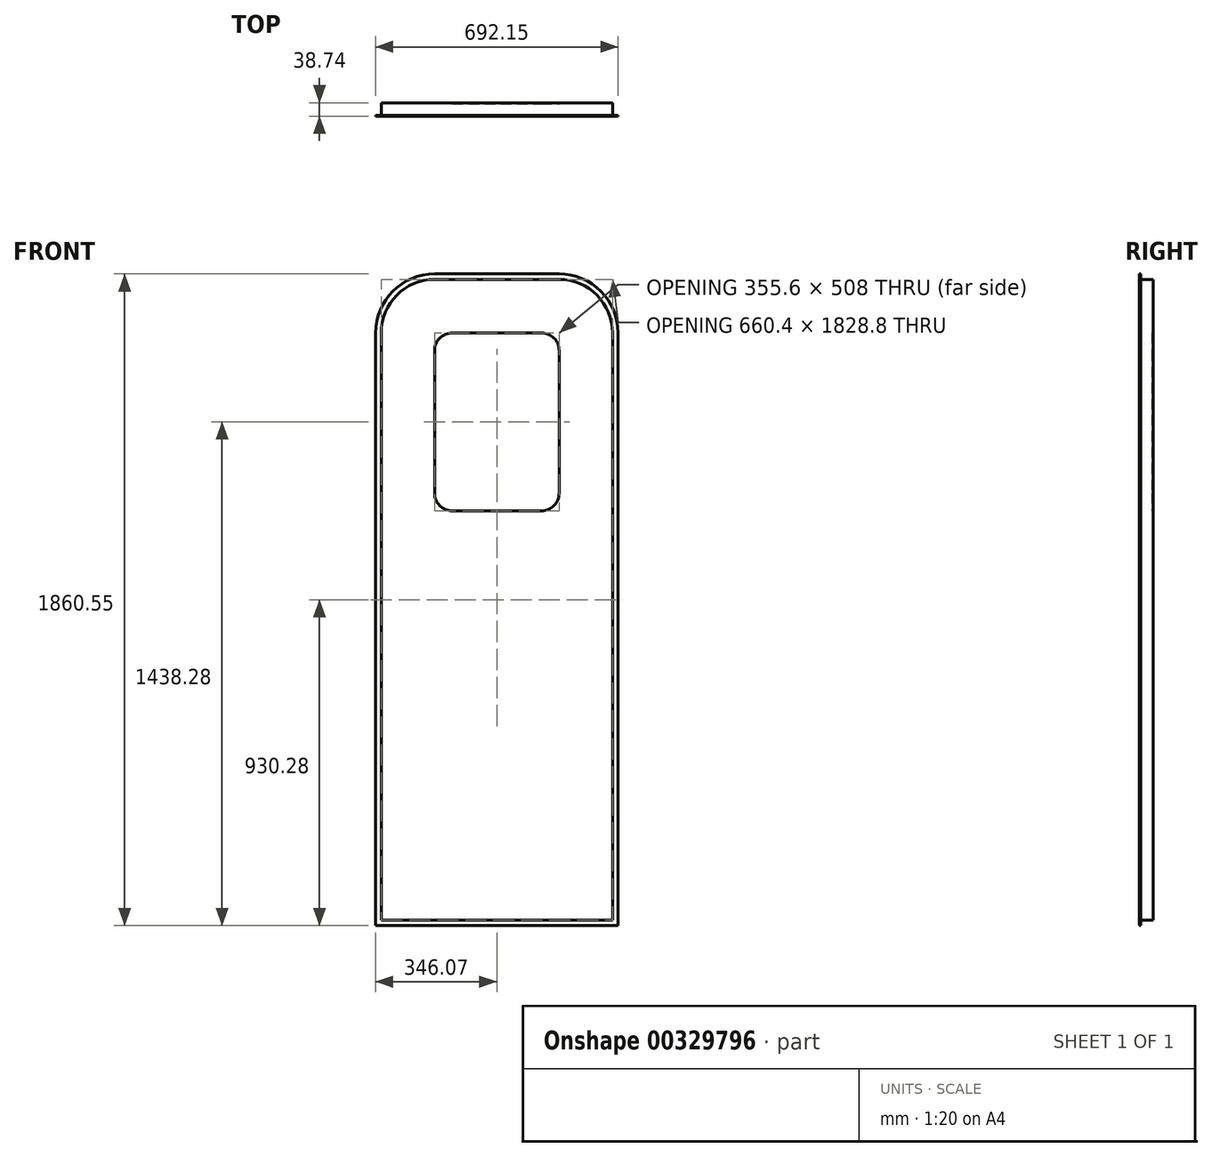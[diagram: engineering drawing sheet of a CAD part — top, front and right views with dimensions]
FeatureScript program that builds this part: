
annotation { "Feature Type Name" : "Feature", "Feature Type Description" : "" }
export const myFeature = defineFeature(function(context is Context, id is Id, definition is map)
    precondition{}
    {
        {
            var Q0;
            Q0=qCreatedBy(makeId("Front.planeOp"),FACE);
            var sketch = newSketch(context, id + "F0", { "sketchPlane" : qUnion([Q0])});
            skLineSegment(sketch, "E0.bottom", {"start": v(0, 0) * mm, "end": v(-660.4, 0) * mm});
            skLineSegment(sketch, "E0.top", {"start": v(-152.4, 1828.8) * mm, "end": v(-508, 1828.8) * mm});
            skLineSegment(sketch, "E0.left", {"start": v(0, 0) * mm, "end": v(0, 1676.4) * mm});
            skLineSegment(sketch, "E0.right", {"start": v(-660.4, 0) * mm, "end": v(-660.4, 1676.4) * mm});
            skPoint(sketch, "E1.visualSharp", {"position": v(-660.4, 1828.8) * mm});
            skArc(sketch, "E1.filletArc", {"start": v(-508, 1828.8) * mm, "mid": v(-615.76, 1784.16) * mm, "end": v(-660.4, 1676.4) * mm});
            skPoint(sketch, "E2.visualSharp", {"position": v(0, 1828.8) * mm});
            skArc(sketch, "E2.filletArc", {"start": v(0, 1676.4) * mm, "mid": v(-44.64, 1784.16) * mm, "end": v(-152.4, 1828.8) * mm});
            skLineSegment(sketch, "E3.0", {"start": v(15.87, -15.87) * mm, "end": v(-676.28, -15.88) * mm});
            skArc(sketch, "E3.1", {"start": v(-508, 1844.67) * mm, "mid": v(-626.99, 1795.39) * mm, "end": v(-676.28, 1676.4) * mm});
            skLineSegment(sketch, "E3.2", {"start": v(-152.4, 1844.67) * mm, "end": v(-508, 1844.67) * mm});
            skLineSegment(sketch, "E3.3", {"start": v(-676.28, -15.87) * mm, "end": v(-676.28, 1676.4) * mm});
            skArc(sketch, "E3.4", {"start": v(15.87, 1676.4) * mm, "mid": v(-33.41, 1795.39) * mm, "end": v(-152.4, 1844.67) * mm});
            skLineSegment(sketch, "E3.5", {"start": v(15.87, -15.87) * mm, "end": v(15.87, 1676.4) * mm});
            skLineSegment(sketch, "E4.bottom", {"start": v(-457.2, 1676.4) * mm, "end": v(-203.2, 1676.4) * mm});
            skLineSegment(sketch, "E4.top", {"start": v(-457.2, 1168.4) * mm, "end": v(-203.2, 1168.4) * mm});
            skLineSegment(sketch, "E4.left", {"start": v(-508, 1625.6) * mm, "end": v(-508, 1219.2) * mm});
            skLineSegment(sketch, "E4.right", {"start": v(-152.4, 1625.6) * mm, "end": v(-152.4, 1219.2) * mm});
            skArc(sketch, "E5.filletArc", {"start": v(-152.4, 1625.6) * mm, "mid": v(-167.28, 1661.52) * mm, "end": v(-203.2, 1676.4) * mm});
            skArc(sketch, "E6.filletArc", {"start": v(-457.2, 1676.4) * mm, "mid": v(-493.12, 1661.52) * mm, "end": v(-508, 1625.6) * mm});
            skPoint(sketch, "E7.visualSharp", {"position": v(-508, 1168.4) * mm});
            skArc(sketch, "E7.filletArc", {"start": v(-508, 1219.2) * mm, "mid": v(-493.12, 1183.28) * mm, "end": v(-457.2, 1168.4) * mm});
            skPoint(sketch, "E8.visualSharp", {"position": v(-152.4, 1168.4) * mm});
            skArc(sketch, "E8.filletArc", {"start": v(-203.2, 1168.4) * mm, "mid": v(-167.28, 1183.28) * mm, "end": v(-152.4, 1219.2) * mm});
            skSolve(sketch);
        }
        {
            var Q0;
            Q0=makeQuery(id+"F0.imprint","IMPRINT",FACE,{"disambiguationData":[TD([[makeQuery(id+"F0.imprint","IMPRINT",EDGE,{"derivedFrom":sQuery(id+"F0.wireOp",EDGE,"E0.bottom")}),-1.0]])]});
            var Q1;
            Q1=makeQuery(id+"F0.imprint","IMPRINT",FACE,{"disambiguationData":[TD([[makeQuery(id+"F0.imprint","IMPRINT",EDGE,{"derivedFrom":sQuery(id+"F0.wireOp",EDGE,"E4.bottom")}),-1.0]])]});
            extrude(context, id + "F1", {"entities" : qUnion([Q0, Q1]), "oppositeDirection" : true, "depth" : 38.1 * mm});
        }
        {
            var Q0;
            Q0=makeQuery(id+"F0.imprint","IMPRINT",FACE,{"disambiguationData":[TD([[makeQuery(id+"F0.imprint","IMPRINT",EDGE,{"derivedFrom":sQuery(id+"F0.wireOp",EDGE,"E0.bottom")}),1.0]])]});
            extrude(context, id + "F2", {"entities" : qUnion([Q0]), "operationType" : NewBodyOperationType.ADD, "oppositeDirection" : true, "depth" : 2.54 * mm, "hasSecondDirection" : true, "secondDirectionOppositeDirection" : false, "secondDirectionDepth" : 0.64 * mm});
        }
        {
            var Q0;
            Q0=makeQuery(id+"F0.imprint","IMPRINT",FACE,{"disambiguationData":[TD([[makeQuery(id+"F0.imprint","IMPRINT",EDGE,{"derivedFrom":sQuery(id+"F0.wireOp",EDGE,"E4.bottom")}),-1.0]])]});
            extrude(context, id + "F3", {"entities" : qUnion([Q0]), "operationType" : NewBodyOperationType.REMOVE, "oppositeDirection" : true, "depth" : 3.17 * mm});
        }
        {
            var Q0;
            Q0=makeQuery(id+"F0.imprint","IMPRINT",FACE,{"disambiguationData":[TD([[makeQuery(id+"F0.imprint","IMPRINT",EDGE,{"derivedFrom":sQuery(id+"F0.wireOp",EDGE,"E4.bottom")}),-1.0]])]});
            extrude(context, id + "F4", {"entities" : qUnion([Q0]), "operationType" : NewBodyOperationType.REMOVE, "oppositeDirection" : true, "depth" : 38.1 * mm, "hasSecondDirection" : true, "secondDirectionOppositeDirection" : true, "secondDirectionDepth" : 34.92 * mm});
        }
    });
